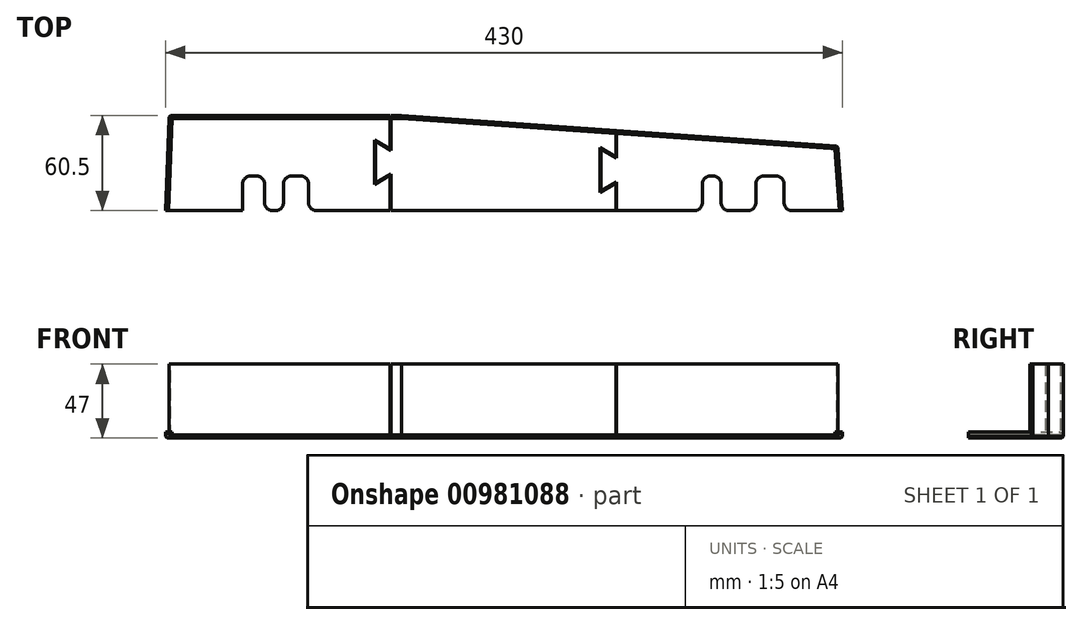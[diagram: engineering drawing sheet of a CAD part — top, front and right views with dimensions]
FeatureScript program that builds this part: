
annotation { "Feature Type Name" : "Feature", "Feature Type Description" : "" }
export const myFeature = defineFeature(function(context is Context, id is Id, definition is map)
    precondition{}
    {
        {
            var Q0;
            Q0=qCreatedBy(makeId("Top.planeOp"),FACE);
            var sketch = newSketch(context, id + "F0", { "sketchPlane" : qUnion([Q0])});
            skLineSegment(sketch, "E0.bottom", {"start": v(0, 0) * mm, "end": v(430, 0) * mm});
            skLineSegment(sketch, "E0.left", {"start": v(0, 0) * mm, "end": v(2.3, 60.5) * mm});
            skLineSegment(sketch, "E1", {"start": v(430, 0) * mm, "end": v(427, 41) * mm});
            skLineSegment(sketch, "E2", {"start": v(427, 41) * mm, "end": v(150, 60.5) * mm});
            skLineSegment(sketch, "E3", {"start": v(150, 60.5) * mm, "end": v(2.3, 60.5) * mm});
            skSolve(sketch);
        }
        {
            var Q0;
            Q0=makeQuery(id+"F0.imprint","IMPRINT",FACE,{"disambiguationData":[TD([[makeQuery(id+"F0.imprint","IMPRINT",EDGE,{"derivedFrom":sQuery(id+"F0.wireOp",EDGE,"E0.bottom")}),1.0]])]});
            extrude(context, id + "F1", {"entities" : qUnion([Q0]), "depth" : 2 * mm, "offsetDistance" : 25 * mm});
        }
        {
            var Q0;
            Q0=makeQuery(id+"F1.opExtrude","CAP_FACE",FACE,{"disambiguationData":[OSD([sQuery(id+"F0.wireOp",EDGE,"E0.bottom"),sQuery(id+"F0.wireOp",EDGE,"E0.left"),sQuery(id+"F0.wireOp",EDGE,"E1"),sQuery(id+"F0.wireOp",EDGE,"E2"),sQuery(id+"F0.wireOp",EDGE,"E3")])],"isStart":false});
            var sketch = newSketch(context, id + "F2", { "sketchPlane" : qUnion([Q0])});
            skLineSegment(sketch, "E4", {"start": v(2.3, 60.5) * mm, "end": v(150, 60.5) * mm});
            skLineSegment(sketch, "E5", {"start": v(150, 60.5) * mm, "end": v(427, 41) * mm});
            skLineSegment(sketch, "E6", {"start": v(427, 41) * mm, "end": v(427.15, 38.98) * mm});
            skLineSegment(sketch, "E7", {"start": v(427.15, 38.98) * mm, "end": v(150, 58.5) * mm});
            skLineSegment(sketch, "E8", {"start": v(150, 58.5) * mm, "end": v(2.22, 58.5) * mm});
            skLineSegment(sketch, "E9", {"start": v(2.3, 60.5) * mm, "end": v(2.22, 58.5) * mm});
            skLineSegment(sketch, "E10", {"start": v(0, 0) * mm, "end": v(2, 0) * mm});
            skLineSegment(sketch, "E11", {"start": v(2, 0) * mm, "end": v(4.23, 58.5) * mm});
            skLineSegment(sketch, "E12", {"start": v(0, 0) * mm, "end": v(2.22, 58.5) * mm});
            skLineSegment(sketch, "E13", {"start": v(427.15, 38.98) * mm, "end": v(430, 0) * mm});
            skLineSegment(sketch, "E14", {"start": v(430, 0) * mm, "end": v(428, 0) * mm});
            skLineSegment(sketch, "E15", {"start": v(428, 0) * mm, "end": v(425.13, 39.13) * mm});
            skSolve(sketch);
        }
        {
            var Q0;
            Q0=makeQuery(id+"F2.imprint","IMPRINT",FACE,{"disambiguationData":[TD([[makeQuery(id+"F2.imprint","IMPRINT",EDGE,{"derivedFrom":sQuery(id+"F2.wireOp",EDGE,"E10")}),1.0]])]});
            var Q1;
            {var subQ0=sQuery(id+"F2.wireOp",EDGE,"E13");Q1=makeQuery(id+"F2.imprint","IMPRINT",FACE,{"disambiguationData":[TD([[makeQuery(id+"F2.imprint","IMPRINT",EDGE,{"derivedFrom":subQ0}),1.0]])]});}
            extrude(context, id + "F3", {"entities" : qUnion([Q0, Q1]), "operationType" : NewBodyOperationType.ADD, "depth" : 2 * mm, "offsetDistance" : 25 * mm});
        }
        {
            var Q0;
            Q0=makeQuery(id+"F2.imprint","IMPRINT",FACE,{"disambiguationData":[TD([[makeQuery(id+"F2.imprint","IMPRINT",EDGE,{"derivedFrom":sQuery(id+"F2.wireOp",EDGE,"E4")}),1.0]])]});
            extrude(context, id + "F4", {"entities" : qUnion([Q0]), "operationType" : NewBodyOperationType.ADD, "depth" : 45 * mm, "offsetDistance" : 25 * mm});
        }
        {
            var Q0;
            {var subQ4=sQuery(id+"F2.wireOp",EDGE,"E11");Q0=makeQuery(id+"F2.imprint","IMPRINT",FACE,{"disambiguationData":[TD([[makeQuery(id+"F2.imprint","IMPRINT",EDGE,{"derivedFrom":subQ4}),-1.0]])]});}
            var sketch = newSketch(context, id + "F5", { "sketchPlane" : qUnion([Q0])});
            skLineSegment(sketch, "E16.bottom", {"start": v(49, 22) * mm, "end": v(63, 22) * mm});
            skLineSegment(sketch, "E16.top", {"start": v(49, 0) * mm, "end": v(63, 0) * mm});
            skLineSegment(sketch, "E16.left", {"start": v(49, 22) * mm, "end": v(49, 0) * mm});
            skLineSegment(sketch, "E16.right", {"start": v(63, 22) * mm, "end": v(63, 0) * mm});
            skLineSegment(sketch, "E17.bottom", {"start": v(75, 22) * mm, "end": v(91, 22) * mm});
            skLineSegment(sketch, "E17.top", {"start": v(75, 0) * mm, "end": v(91, 0) * mm});
            skLineSegment(sketch, "E17.left", {"start": v(75, 22) * mm, "end": v(75, 0) * mm});
            skLineSegment(sketch, "E17.right", {"start": v(91, 22) * mm, "end": v(91, 0) * mm});
            skLineSegment(sketch, "E18.bottom", {"start": v(341, 22) * mm, "end": v(353, 22) * mm});
            skLineSegment(sketch, "E18.top", {"start": v(341, 0) * mm, "end": v(353, 0) * mm});
            skLineSegment(sketch, "E18.left", {"start": v(341, 22) * mm, "end": v(341, 0) * mm});
            skLineSegment(sketch, "E18.right", {"start": v(353, 22) * mm, "end": v(353, 0) * mm});
            skLineSegment(sketch, "E19.bottom", {"start": v(375, 22) * mm, "end": v(393, 22) * mm});
            skLineSegment(sketch, "E19.top", {"start": v(375, 0) * mm, "end": v(393, 0) * mm});
            skLineSegment(sketch, "E19.left", {"start": v(375, 22) * mm, "end": v(375, 0) * mm});
            skLineSegment(sketch, "E19.right", {"start": v(393, 22) * mm, "end": v(393, 0) * mm});
            skSolve(sketch);
        }
        {
            var Q0;
            Q0 = qSketchRegion(id + "F5", true);
            extrude(context, id + "F6", {"entities" : qUnion([Q0]), "operationType" : NewBodyOperationType.REMOVE, "oppositeDirection" : true, "depth" : 25 * mm, "offsetDistance" : 25 * mm});
        }
        {
            var Q0;
            Q0=makeQuery(id+"F6.boolean.opBoolean","COPY",EDGE,{"derivedFrom":makeQuery(id+"F6.opExtrude","SWEPT_EDGE",EDGE,{"disambiguationData":[OSD([sQuery(id+"F5.wireOp",EDGE,"E16.bottom"),sQuery(id+"F5.wireOp",EDGE,"E16.left")])]})});
            var Q1;
            Q1=makeQuery(id+"F6.boolean.opBoolean","COPY",EDGE,{"derivedFrom":makeQuery(id+"F6.opExtrude","SWEPT_EDGE",EDGE,{"disambiguationData":[OSD([sQuery(id+"F5.wireOp",EDGE,"E16.bottom"),sQuery(id+"F5.wireOp",EDGE,"E16.right")])]})});
            var Q2;
            Q2=makeQuery(id+"F6.boolean.opBoolean","COPY",EDGE,{"derivedFrom":makeQuery(id+"F6.opExtrude","SWEPT_EDGE",EDGE,{"disambiguationData":[OSD([sQuery(id+"F5.wireOp",EDGE,"E17.bottom"),sQuery(id+"F5.wireOp",EDGE,"E17.left")])]})});
            var Q3;
            Q3=makeQuery(id+"F6.boolean.opBoolean","COPY",EDGE,{"derivedFrom":makeQuery(id+"F6.opExtrude","SWEPT_EDGE",EDGE,{"disambiguationData":[OSD([sQuery(id+"F5.wireOp",EDGE,"E17.bottom"),sQuery(id+"F5.wireOp",EDGE,"E17.right")])]})});
            var Q4;
            Q4=makeQuery(id+"F6.boolean.opBoolean","COPY",EDGE,{"derivedFrom":makeQuery(id+"F6.opExtrude","SWEPT_EDGE",EDGE,{"disambiguationData":[OSD([sQuery(id+"F0.wireOp",EDGE,"E0.bottom"),sQuery(id+"F5.wireOp",EDGE,"E16.top"),sQuery(id+"F5.wireOp",EDGE,"E16.left")])]})});
            var Q5;
            Q5=makeQuery(id+"F6.boolean.opBoolean","COPY",EDGE,{"derivedFrom":makeQuery(id+"F6.opExtrude","SWEPT_EDGE",EDGE,{"disambiguationData":[OSD([sQuery(id+"F0.wireOp",EDGE,"E0.bottom"),sQuery(id+"F5.wireOp",EDGE,"E16.top"),sQuery(id+"F5.wireOp",EDGE,"E16.right")])]})});
            var Q6;
            Q6=makeQuery(id+"F6.boolean.opBoolean","COPY",EDGE,{"derivedFrom":makeQuery(id+"F6.opExtrude","SWEPT_EDGE",EDGE,{"disambiguationData":[OSD([sQuery(id+"F0.wireOp",EDGE,"E0.bottom"),sQuery(id+"F5.wireOp",EDGE,"E17.top"),sQuery(id+"F5.wireOp",EDGE,"E17.left")])]})});
            var Q7;
            Q7=makeQuery(id+"F6.boolean.opBoolean","COPY",EDGE,{"derivedFrom":makeQuery(id+"F6.opExtrude","SWEPT_EDGE",EDGE,{"disambiguationData":[OSD([sQuery(id+"F0.wireOp",EDGE,"E0.bottom"),sQuery(id+"F5.wireOp",EDGE,"E17.top"),sQuery(id+"F5.wireOp",EDGE,"E17.right")])]})});
            var Q8;
            Q8=makeQuery(id+"F6.boolean.opBoolean","COPY",EDGE,{"derivedFrom":makeQuery(id+"F6.opExtrude","SWEPT_EDGE",EDGE,{"disambiguationData":[OSD([sQuery(id+"F0.wireOp",EDGE,"E0.bottom"),sQuery(id+"F5.wireOp",EDGE,"E19.top"),sQuery(id+"F5.wireOp",EDGE,"E19.right")])]})});
            var Q9;
            Q9=makeQuery(id+"F6.boolean.opBoolean","COPY",EDGE,{"derivedFrom":makeQuery(id+"F6.opExtrude","SWEPT_EDGE",EDGE,{"disambiguationData":[OSD([sQuery(id+"F5.wireOp",EDGE,"E19.bottom"),sQuery(id+"F5.wireOp",EDGE,"E19.right")])]})});
            var Q10;
            Q10=makeQuery(id+"F6.boolean.opBoolean","COPY",EDGE,{"derivedFrom":makeQuery(id+"F6.opExtrude","SWEPT_EDGE",EDGE,{"disambiguationData":[OSD([sQuery(id+"F0.wireOp",EDGE,"E0.bottom"),sQuery(id+"F5.wireOp",EDGE,"E19.top"),sQuery(id+"F5.wireOp",EDGE,"E19.left")])]})});
            var Q11;
            Q11=makeQuery(id+"F6.boolean.opBoolean","COPY",EDGE,{"derivedFrom":makeQuery(id+"F6.opExtrude","SWEPT_EDGE",EDGE,{"disambiguationData":[OSD([sQuery(id+"F0.wireOp",EDGE,"E0.bottom"),sQuery(id+"F5.wireOp",EDGE,"E18.top"),sQuery(id+"F5.wireOp",EDGE,"E18.right")])]})});
            var Q12;
            Q12=makeQuery(id+"F6.boolean.opBoolean","COPY",EDGE,{"derivedFrom":makeQuery(id+"F6.opExtrude","SWEPT_EDGE",EDGE,{"disambiguationData":[OSD([sQuery(id+"F0.wireOp",EDGE,"E0.bottom"),sQuery(id+"F5.wireOp",EDGE,"E18.top"),sQuery(id+"F5.wireOp",EDGE,"E18.left")])]})});
            var Q13;
            Q13=makeQuery(id+"F6.boolean.opBoolean","COPY",EDGE,{"derivedFrom":makeQuery(id+"F6.opExtrude","SWEPT_EDGE",EDGE,{"disambiguationData":[OSD([sQuery(id+"F5.wireOp",EDGE,"E18.bottom"),sQuery(id+"F5.wireOp",EDGE,"E18.right")])]})});
            var Q14;
            Q14=makeQuery(id+"F6.boolean.opBoolean","COPY",EDGE,{"derivedFrom":makeQuery(id+"F6.opExtrude","SWEPT_EDGE",EDGE,{"disambiguationData":[OSD([sQuery(id+"F5.wireOp",EDGE,"E19.bottom"),sQuery(id+"F5.wireOp",EDGE,"E19.left")])]})});
            var Q15;
            Q15=makeQuery(id+"F6.boolean.opBoolean","COPY",EDGE,{"derivedFrom":makeQuery(id+"F6.opExtrude","SWEPT_EDGE",EDGE,{"disambiguationData":[OSD([sQuery(id+"F5.wireOp",EDGE,"E18.bottom"),sQuery(id+"F5.wireOp",EDGE,"E18.left")])]})});
            fillet(context, id + "F7", {"entities" : qUnion([Q0, Q1, Q2, Q3, Q4, Q5, Q6, Q7, Q8, Q9, Q10, Q11, Q12, Q13, Q14, Q15]), "radius" : 5 * mm, "tangentPropagation" : true, "allowEdgeOverflow" : false});
        }
        {
            var Q0;
            Q0=makeQuery(id+"F1.opExtrude","CAP_EDGE",EDGE,{"disambiguationData":[OSD([sQuery(id+"F0.wireOp",EDGE,"E1")])],"isStart":true});
            var Q1;
            Q1=makeQuery(id+"F1.opExtrude","CAP_EDGE",EDGE,{"disambiguationData":[OSD([sQuery(id+"F0.wireOp",EDGE,"E2")])],"isStart":true});
            var Q2;
            Q2=makeQuery(id+"F1.opExtrude","CAP_EDGE",EDGE,{"disambiguationData":[OSD([sQuery(id+"F0.wireOp",EDGE,"E3")])],"isStart":true});
            var Q3;
            Q3=makeQuery(id+"F1.opExtrude","CAP_EDGE",EDGE,{"disambiguationData":[OSD([sQuery(id+"F0.wireOp",EDGE,"E0.left")])],"isStart":true});
            var Q4;
            Q4=makeQuery(id+"F4.boolean.opBoolean","MERGE",EDGE,{"derivedFrom":[makeQuery(id+"F1.opExtrude","SWEPT_EDGE",EDGE,{"disambiguationData":[OSD([sQuery(id+"F0.wireOp",EDGE,"E0.left"),sQuery(id+"F0.wireOp",EDGE,"E3")])]}),makeQuery(id+"F4.opExtrude","SWEPT_EDGE",EDGE,{"disambiguationData":[OSD([sQuery(id+"F2.wireOp",EDGE,"E4"),sQuery(id+"F2.wireOp",EDGE,"E9")])]})]});
            var Q5;
            Q5=makeQuery(id+"F4.boolean.opBoolean","MERGE",EDGE,{"derivedFrom":[makeQuery(id+"F1.opExtrude","SWEPT_EDGE",EDGE,{"disambiguationData":[OSD([sQuery(id+"F0.wireOp",EDGE,"E1"),sQuery(id+"F0.wireOp",EDGE,"E2")])]}),makeQuery(id+"F4.opExtrude","SWEPT_EDGE",EDGE,{"disambiguationData":[OSD([sQuery(id+"F2.wireOp",EDGE,"E5"),sQuery(id+"F2.wireOp",EDGE,"E6")])]})]});
            var Q6;
            Q6=makeQuery(id+"F3.opExtrude","CAP_EDGE",EDGE,{"disambiguationData":[OSD([sQuery(id+"F2.wireOp",EDGE,"E11")])],"isStart":true});
            var Q7;
            Q7=makeQuery(id+"F4.opExtrude","CAP_EDGE",EDGE,{"disambiguationData":[OSD([sQuery(id+"F2.wireOp",EDGE,"E8")])],"isStart":true});
            var Q8;
            Q8=makeQuery(id+"F4.opExtrude","CAP_EDGE",EDGE,{"disambiguationData":[OSD([sQuery(id+"F2.wireOp",EDGE,"E7")])],"isStart":true});
            var Q9;
            Q9=makeQuery(id+"F3.opExtrude","CAP_EDGE",EDGE,{"disambiguationData":[OSD([sQuery(id+"F2.wireOp",EDGE,"E15")])],"isStart":true});
            var Q10;
            Q10=makeQuery(id+"F3.opExtrude","SWEPT_EDGE",EDGE,{"disambiguationData":[OSD([sQuery(id+"F2.wireOp",EDGE,"E8"),sQuery(id+"F2.wireOp",EDGE,"E11")])]});
            var Q11;
            Q11=makeQuery(id+"F3.opExtrude","CAP_EDGE",EDGE,{"disambiguationData":[OSD([sQuery(id+"F2.wireOp",EDGE,"E8")])],"isStart":false});
            var Q12;
            Q12=makeQuery(id+"F3.opExtrude","CAP_EDGE",EDGE,{"disambiguationData":[OSD([sQuery(id+"F2.wireOp",EDGE,"E7")])],"isStart":false});
            var Q13;
            Q13=makeQuery(id+"F3.opExtrude","SWEPT_EDGE",EDGE,{"disambiguationData":[OSD([sQuery(id+"F2.wireOp",EDGE,"E7"),sQuery(id+"F2.wireOp",EDGE,"E15")])]});
            chamfer(context, id + "F8", {"entities" : qUnion([Q0, Q1, Q2, Q3, Q4, Q5, Q6, Q7, Q8, Q9, Q10, Q11, Q12, Q13]), "width" : 1 * mm, "tangentPropagation" : true});
        }
        {
            var Q0;
            {var subQ4=sQuery(id+"F2.wireOp",EDGE,"E11");Q0=makeQuery(id+"F2.imprint","IMPRINT",FACE,{"disambiguationData":[TD([[makeQuery(id+"F2.imprint","IMPRINT",EDGE,{"derivedFrom":subQ4}),-1.0]])]});}
            var sketch = newSketch(context, id + "F9", { "sketchPlane" : qUnion([Q0])});
            skLineSegment(sketch, "E20", {"start": v(143.33, 60.97) * mm, "end": v(143.33, 38.34) * mm});
            skLineSegment(sketch, "E21", {"start": v(143.33, 38.34) * mm, "end": v(133.33, 44.11) * mm});
            skLineSegment(sketch, "E22", {"start": v(133.33, 44.11) * mm, "end": v(133.33, 17.56) * mm});
            skLineSegment(sketch, "E23", {"start": v(133.33, 17.56) * mm, "end": v(143.33, 23.34) * mm});
            skLineSegment(sketch, "E24", {"start": v(143.33, 23.34) * mm, "end": v(143.33, 0) * mm});
            skLineSegment(sketch, "E25", {"start": v(133.33, 17.56) * mm, "end": v(133.33, 0) * mm, "construction": true});
            skLineSegment(sketch, "E26", {"start": v(133.33, 44.11) * mm, "end": v(133.33, 61.67) * mm, "construction": true});
            skLineSegment(sketch, "E27.0", {"start": v(142.83, 22.47) * mm, "end": v(142.83, 0) * mm});
            skLineSegment(sketch, "E27.1", {"start": v(142.83, 61) * mm, "end": v(142.83, 39.2) * mm});
            skLineSegment(sketch, "E27.2", {"start": v(142.83, 39.2) * mm, "end": v(132.83, 44.98) * mm});
            skLineSegment(sketch, "E27.3", {"start": v(132.83, 44.98) * mm, "end": v(132.83, 16.7) * mm});
            skLineSegment(sketch, "E27.4", {"start": v(132.83, 16.7) * mm, "end": v(142.83, 22.47) * mm});
            skLineSegment(sketch, "E28", {"start": v(143.33, 60.97) * mm, "end": v(142.83, 61) * mm});
            skLineSegment(sketch, "E29", {"start": v(143.33, 0) * mm, "end": v(142.83, 0) * mm});
            skLineSegment(sketch, "E30", {"start": v(286.67, 50.88) * mm, "end": v(286.67, 33.3) * mm});
            skLineSegment(sketch, "E31", {"start": v(286.67, 33.3) * mm, "end": v(276.67, 39.07) * mm});
            skLineSegment(sketch, "E32", {"start": v(276.67, 39.07) * mm, "end": v(276.67, 12.52) * mm});
            skLineSegment(sketch, "E33", {"start": v(276.67, 12.52) * mm, "end": v(286.67, 18.3) * mm});
            skLineSegment(sketch, "E34", {"start": v(286.67, 18.3) * mm, "end": v(286.67, 0) * mm});
            skLineSegment(sketch, "E35", {"start": v(276.67, 12.52) * mm, "end": v(276.67, 0) * mm, "construction": true});
            skLineSegment(sketch, "E36", {"start": v(276.67, 39.07) * mm, "end": v(276.67, 51.58) * mm, "construction": true});
            skLineSegment(sketch, "E37.0", {"start": v(286.17, 17.43) * mm, "end": v(286.17, 0) * mm});
            skLineSegment(sketch, "E37.1", {"start": v(286.17, 50.88) * mm, "end": v(286.17, 34.16) * mm});
            skLineSegment(sketch, "E37.2", {"start": v(286.17, 34.16) * mm, "end": v(276.17, 39.93) * mm});
            skLineSegment(sketch, "E37.3", {"start": v(276.17, 39.93) * mm, "end": v(276.17, 11.65) * mm});
            skLineSegment(sketch, "E37.4", {"start": v(276.17, 11.65) * mm, "end": v(286.17, 17.43) * mm});
            skLineSegment(sketch, "E38", {"start": v(286.67, 50.88) * mm, "end": v(286.17, 50.88) * mm});
            skLineSegment(sketch, "E39", {"start": v(286.67, 0) * mm, "end": v(286.17, 0) * mm});
            skSolve(sketch);
        }
        {
            var Q0;
            Q0 = qSketchRegion(id + "F9", true);
            extrude(context, id + "F10", {"entities" : qUnion([Q0]), "operationType" : NewBodyOperationType.REMOVE, "endBound" : BoundingType.THROUGH_ALL, "oppositeDirection" : true, "depth" : 25 * mm, "offsetDistance" : 25 * mm, "hasSecondDirection" : true, "secondDirectionBound" : SecondDirectionBoundingType.THROUGH_ALL, "secondDirectionOppositeDirection" : false, "secondDirectionDepth" : 25 * mm});
        }
    });
